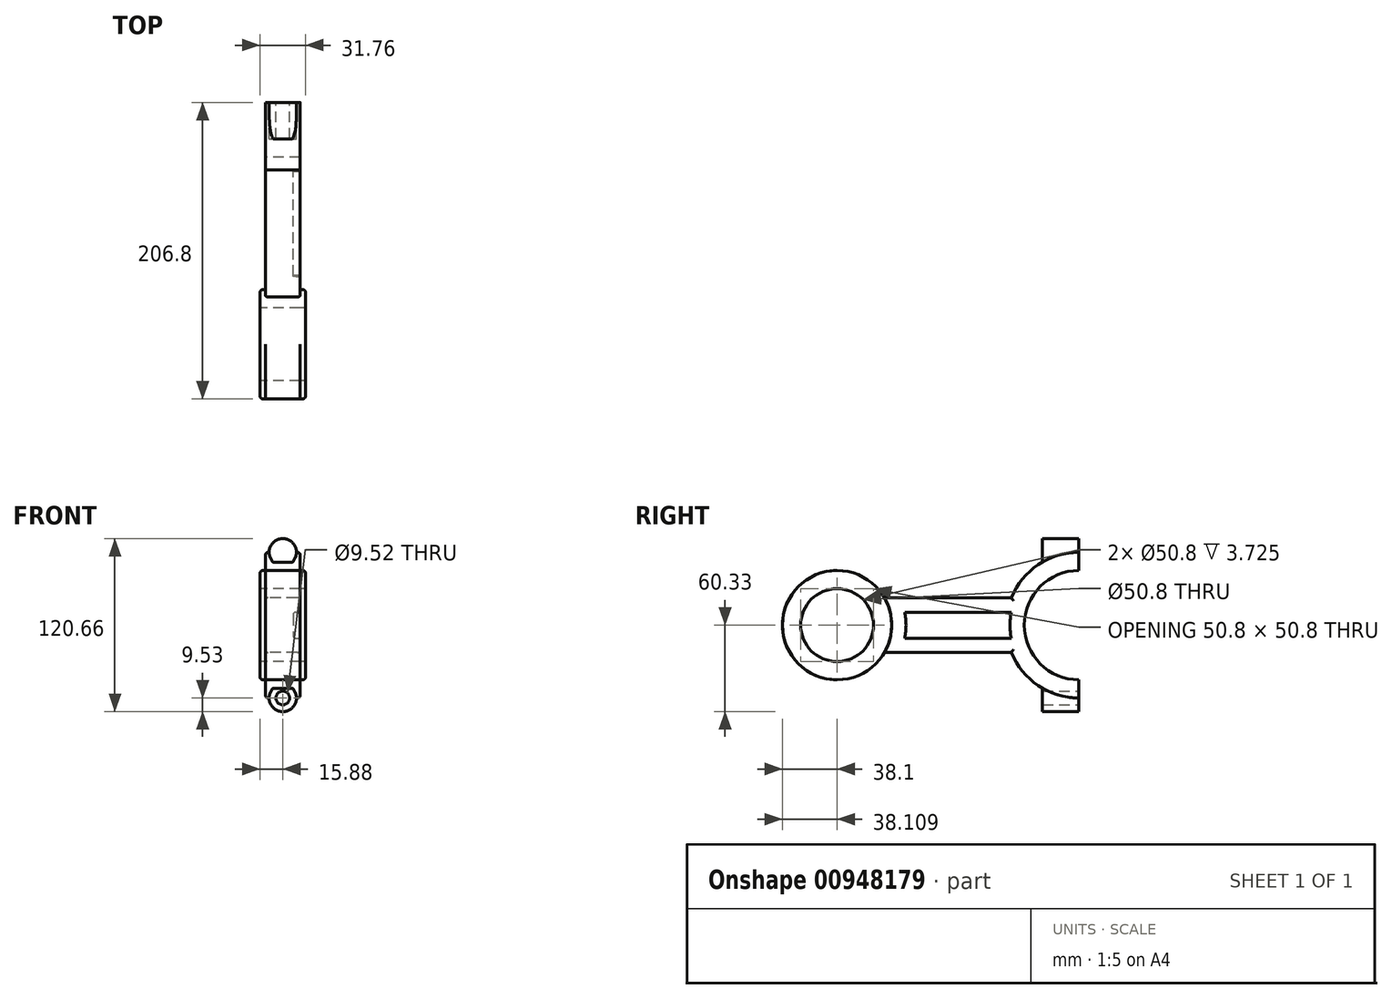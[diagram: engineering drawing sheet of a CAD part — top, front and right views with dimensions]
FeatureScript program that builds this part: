
annotation { "Feature Type Name" : "Feature", "Feature Type Description" : "" }
export const myFeature = defineFeature(function(context is Context, id is Id, definition is map)
    precondition{}
    {
        {
            var Q0;
            Q0=qCreatedBy(makeId("Right.planeOp"),FACE);
            var sketch = newSketch(context, id + "F0", { "sketchPlane" : qUnion([Q0])});
            skLineSegment(sketch, "E0.bottom", {"start": v(29.1, -19.05) * mm, "end": v(-76.2, -19.05) * mm});
            skLineSegment(sketch, "E0.top", {"start": v(29.1, 19.05) * mm, "end": v(-76.2, 19.05) * mm});
            skLineSegment(sketch, "E0.left", {"start": v(76.2, -19.05) * mm, "end": v(76.2, 19.05) * mm});
            skLineSegment(sketch, "E0.right", {"start": v(-76.2, -19.05) * mm, "end": v(-76.2, 19.05) * mm});
            skPoint(sketch, "E0.middle", {"position": v(0, 0) * mm});
            skCircle(sketch, "E1", {"center": v(-92.5, 0) * mm, "radius": 25.4 * mm});
            skCircle(sketch, "E2.0", {"center": v(-92.5, 0) * mm, "radius": 38.1 * mm});
            skArc(sketch, "E3", {"start": v(76.2, 38.1) * mm, "mid": v(38.1, 0) * mm, "end": v(76.2, -38.1) * mm});
            skArc(sketch, "E4.0", {"start": v(76.2, 50.8) * mm, "mid": v(47.8, 42.12) * mm, "end": v(29.1, 19.05) * mm});
            skPoint(sketch, "E5", {"position": v(106.26, 0) * mm});
            skLineSegment(sketch, "E6", {"start": v(76.2, 110.37) * mm, "end": v(76.2, -139.44) * mm, "construction": true});
            skPoint(sketch, "E7.end.orphan", {"position": v(136.32, 0) * mm});
            skArc(sketch, "E8.trimOffspring", {"start": v(29.1, -19.05) * mm, "mid": v(47.8, -42.12) * mm, "end": v(76.2, -50.8) * mm});
            skLineSegment(sketch, "E9", {"start": v(76.2, 38.1) * mm, "end": v(76.2, 50.8) * mm});
            skLineSegment(sketch, "E10", {"start": v(76.2, -50.8) * mm, "end": v(76.2, -38.1) * mm});
            skSolve(sketch);
        }
        {
            var Q0;
            Q0 = qSketchRegion(id + "F0", true);
            extrude(context, id + "F1", {"entities" : qUnion([Q0]), "endBound" : BoundingType.SYMMETRIC, "depth" : 24.3 * mm, "offsetDistance" : 25 * mm});
        }
        {
            var Q0;
            Q0=qCreatedBy(makeId("Right.planeOp"),FACE);
            var sketch = newSketch(context, id + "F2", { "sketchPlane" : qUnion([Q0])});
            skCircle(sketch, "E11", {"center": v(-92.5, 0) * mm, "radius": 25.4 * mm});
            skCircle(sketch, "E12.0", {"center": v(-92.5, 0) * mm, "radius": 38.1 * mm});
            skSolve(sketch);
        }
        {
            var Q0;
            Q0 = qSketchRegion(id + "F2", true);
            extrude(context, id + "F3", {"entities" : qUnion([Q0]), "operationType" : NewBodyOperationType.ADD, "endBound" : BoundingType.SYMMETRIC, "depth" : 31.75 * mm, "offsetDistance" : 25 * mm});
        }
        {
            var Q0;
            Q0=makeQuery(id+"F1.opExtrude","SWEPT_FACE",FACE,{"disambiguationData":[OSD([sQuery(id+"F0.wireOp",EDGE,"E10")])]});
            var sketch = newSketch(context, id + "F4", { "sketchPlane" : qUnion([Q0])});
            skPoint(sketch, "E13", {"position": v(0, 50.8) * mm});
            skPoint(sketch, "E14", {"position": v(0, -50.8) * mm});
            skCircle(sketch, "E15", {"center": v(0, -50.8) * mm, "radius": 9.53 * mm});
            skCircle(sketch, "E16", {"center": v(0, 50.8) * mm, "radius": 9.53 * mm});
            skSolve(sketch);
        }
        {
            var Q0;
            Q0 = qSketchRegion(id + "F4", true);
            extrude(context, id + "F5", {"entities" : qUnion([Q0]), "operationType" : NewBodyOperationType.ADD, "oppositeDirection" : true, "depth" : 25.4 * mm, "offsetDistance" : 25 * mm});
        }
        {
            var Q0;
            Q0=makeQuery(id+"F5.boolean.opBoolean","MERGE",FACE,{"derivedFrom":[makeQuery(id+"F1.opExtrude","SWEPT_FACE",FACE,{"disambiguationData":[OSD([sQuery(id+"F0.wireOp",EDGE,"E10")])]}),makeQuery(id+"F5.opExtrude","CAP_FACE",FACE,{"disambiguationData":[OSD([sQuery(id+"F4.wireOp",EDGE,"E15")])],"isStart":true})]});
            var sketch = newSketch(context, id + "F6", { "sketchPlane" : qUnion([Q0])});
            skCircle(sketch, "E17", {"center": v(0, -50.8) * mm, "radius": 4.76 * mm});
            skSolve(sketch);
        }
        {
            var Q0;
            Q0 = qSketchRegion(id + "F6", true);
            extrude(context, id + "F7", {"entities" : qUnion([Q0]), "operationType" : NewBodyOperationType.REMOVE, "oppositeDirection" : true, "depth" : 40 * mm, "offsetDistance" : 25 * mm});
        }
        {
            var Q0;
            {var subQ0=sQuery(id+"F0.wireOp",EDGE,"E4.0");var subQ1=sQuery(id+"F0.wireOp",EDGE,"E3");var subQ2=sQuery(id+"F0.wireOp",EDGE,"E0.top");var subQ3=sQuery(id+"F0.wireOp",EDGE,"E0.bottom");var subQ4=sQuery(id+"F0.wireOp",EDGE,"E8.trimOffspring");var subQ5=sQuery(id+"F0.wireOp",EDGE,"E9");var subQ6=sQuery(id+"F0.wireOp",EDGE,"E10");Q0=makeQuery(id+"F3.boolean.opBoolean","SPLIT",FACE,{"disambiguationData":[TD([makeQuery(id+"F1.opExtrude","SWEPT_FACE",FACE,{"disambiguationData":[OSD([subQ3])]})])],"derivedFrom":makeQuery(id+"F1.opExtrude","CAP_FACE",FACE,{"disambiguationData":[OSD([subQ3,subQ2,sQuery(id+"F0.wireOp",EDGE,"E1"),sQuery(id+"F0.wireOp",EDGE,"E2.0"),subQ1,subQ0,subQ4,subQ5,subQ6])],"isStart":false})});}
            var sketch = newSketch(context, id + "F8", { "sketchPlane" : qUnion([Q0])});
            skLineSegment(sketch, "E18.0", {"start": v(28.96, 9.05) * mm, "end": v(-45.25, 9.05) * mm});
            skArc(sketch, "E18.1", {"start": v(28.96, -9.05) * mm, "mid": v(28.1, 0) * mm, "end": v(28.96, 9.05) * mm});
            skLineSegment(sketch, "E18.2", {"start": v(-45.25, -9.05) * mm, "end": v(28.96, -9.05) * mm});
            skArc(sketch, "E18.3", {"start": v(-45.25, 9.05) * mm, "mid": v(-44.4, 0) * mm, "end": v(-45.25, -9.05) * mm});
            skSolve(sketch);
        }
        {
            var Q0;
            Q0=makeQuery(id+"F8.imprint","IMPRINT",FACE,{"disambiguationData":[TD([[makeQuery(id+"F8.imprint","IMPRINT",EDGE,{"derivedFrom":sQuery(id+"F8.wireOp",EDGE,"E18.0")}),1.0]])]});
            extrude(context, id + "F9", {"entities" : qUnion([Q0]), "operationType" : NewBodyOperationType.REMOVE, "oppositeDirection" : true, "depth" : 5 * mm, "offsetDistance" : 25 * mm});
        }
        {
            var Q0;
            Q0=makeQuery(id+"F3.opExtrude","CAP_EDGE",EDGE,{"disambiguationData":[OSD([sQuery(id+"F2.wireOp",EDGE,"E12.0")])],"isStart":false});
            var Q1;
            Q1=makeQuery(id+"F3.opExtrude","CAP_EDGE",EDGE,{"disambiguationData":[OSD([sQuery(id+"F2.wireOp",EDGE,"E12.0")])],"isStart":true});
            var Q2;
            Q2=makeQuery(id+"F1.opExtrude","CAP_EDGE",EDGE,{"disambiguationData":[OSD([sQuery(id+"F0.wireOp",EDGE,"E0.bottom")])],"isStart":false});
            var Q3;
            Q3=makeQuery(id+"F1.opExtrude","CAP_EDGE",EDGE,{"disambiguationData":[OSD([sQuery(id+"F0.wireOp",EDGE,"E0.top")])],"isStart":false});
            var Q4;
            Q4=makeQuery(id+"F1.opExtrude","CAP_EDGE",EDGE,{"disambiguationData":[OSD([sQuery(id+"F0.wireOp",EDGE,"E0.top")])],"isStart":true});
            var Q5;
            Q5=makeQuery(id+"F1.opExtrude","CAP_EDGE",EDGE,{"disambiguationData":[OSD([sQuery(id+"F0.wireOp",EDGE,"E0.bottom")])],"isStart":true});
            var Q6;
            Q6=makeQuery(id+"F1.opExtrude","CAP_EDGE",EDGE,{"disambiguationData":[OSD([sQuery(id+"F0.wireOp",EDGE,"E4.0")])],"isStart":true});
            var Q7;
            Q7=makeQuery(id+"F1.opExtrude","CAP_EDGE",EDGE,{"disambiguationData":[OSD([sQuery(id+"F0.wireOp",EDGE,"E4.0")])],"isStart":false});
            var Q8;
            Q8=makeQuery(id+"F1.opExtrude","CAP_EDGE",EDGE,{"disambiguationData":[OSD([sQuery(id+"F0.wireOp",EDGE,"E8.trimOffspring")])],"isStart":true});
            var Q9;
            Q9=makeQuery(id+"F1.opExtrude","CAP_EDGE",EDGE,{"disambiguationData":[OSD([sQuery(id+"F0.wireOp",EDGE,"E8.trimOffspring")])],"isStart":false});
            var Q10;
            Q10=makeQuery(id+"F9.boolean.opBoolean","COPY",EDGE,{"derivedFrom":makeQuery(id+"F9.opExtrude","CAP_EDGE",EDGE,{"disambiguationData":[OSD([sQuery(id+"F8.wireOp",EDGE,"E18.0")])],"isStart":false})});
            var Q11;
            Q11=makeQuery(id+"F9.boolean.opBoolean","COPY",EDGE,{"derivedFrom":makeQuery(id+"F9.opExtrude","CAP_EDGE",EDGE,{"disambiguationData":[OSD([sQuery(id+"F8.wireOp",EDGE,"E18.2")])],"isStart":false})});
            var Q12;
            Q12=makeQuery(id+"F19KElKSepnQm7V_1.1.F9.boolean.opBoolean","COPY",EDGE,{"derivedFrom":makeQuery(id+"F19KElKSepnQm7V_1.1.F9.opExtrude","CAP_EDGE",EDGE,{"disambiguationData":[OSD([sQuery(id+"F8.wireOp",EDGE,"E18.2")])],"isStart":false})});
            var Q13;
            Q13=makeQuery(id+"F19KElKSepnQm7V_1.1.F9.boolean.opBoolean","COPY",EDGE,{"derivedFrom":makeQuery(id+"F19KElKSepnQm7V_1.1.F9.opExtrude","CAP_EDGE",EDGE,{"disambiguationData":[OSD([sQuery(id+"F8.wireOp",EDGE,"E18.0")])],"isStart":false})});
            fillet(context, id + "F10", {"entities" : qUnion([Q0, Q1, Q2, Q3, Q4, Q5, Q6, Q7, Q8, Q9, Q10, Q11, Q12, Q13]), "radius" : 2 * mm, "tangentPropagation" : true, "allowEdgeOverflow" : false});
        }
    });
